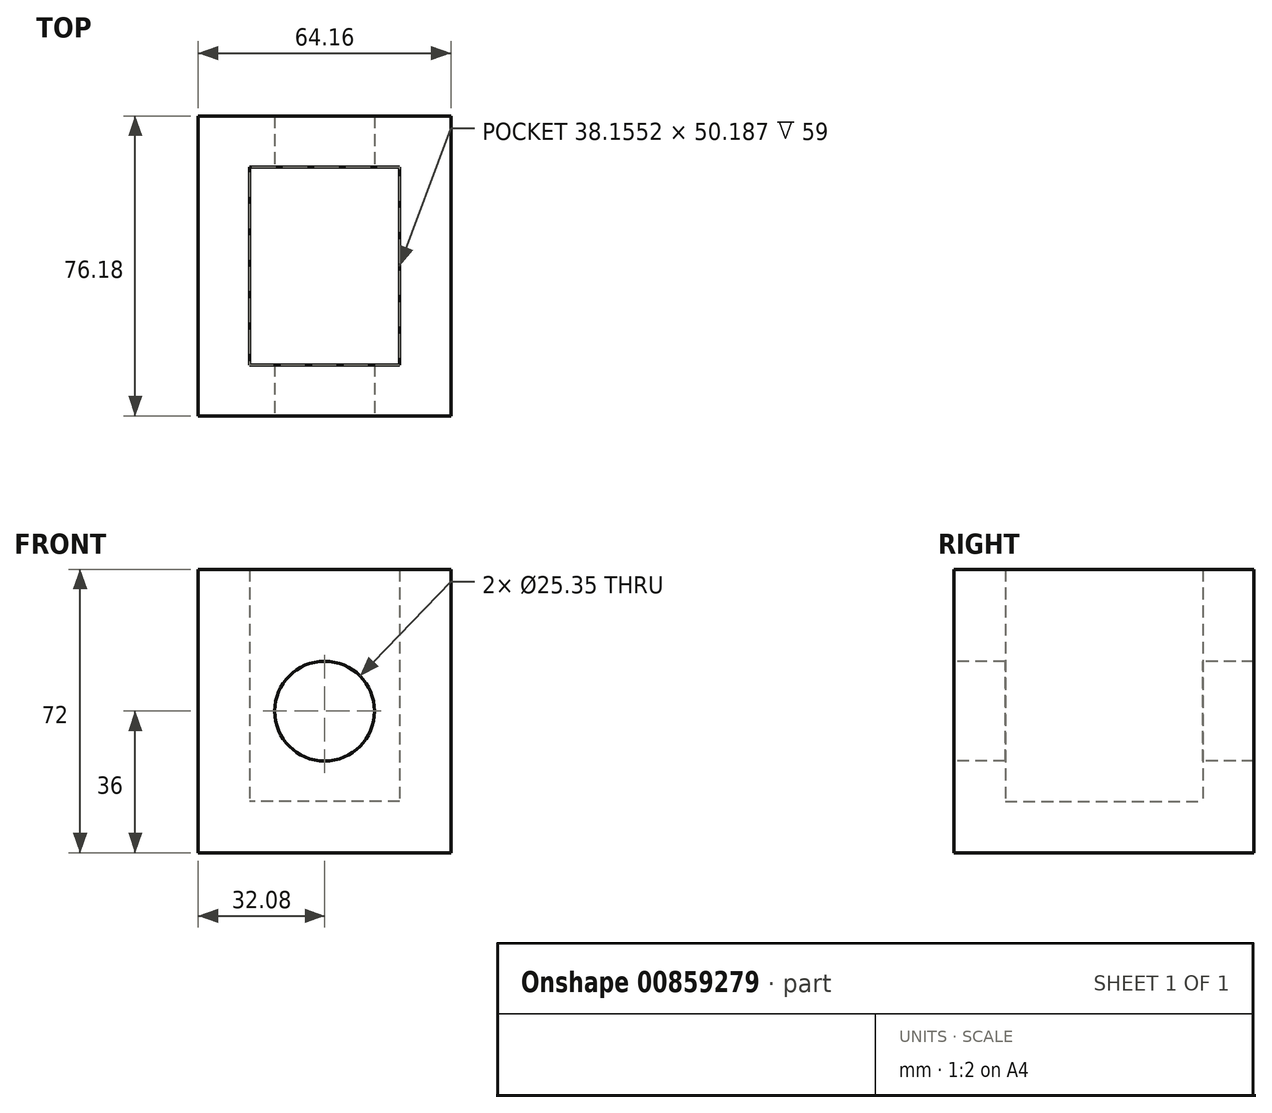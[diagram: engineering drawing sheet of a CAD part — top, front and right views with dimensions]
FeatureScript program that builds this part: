
annotation { "Feature Type Name" : "Feature", "Feature Type Description" : "" }
export const myFeature = defineFeature(function(context is Context, id is Id, definition is map)
    precondition{}
    {
        {
            var Q0;
            Q0=qCreatedBy(makeId("Top.planeOp"),FACE);
            var sketch = newSketch(context, id + "F0", { "sketchPlane" : qUnion([Q0])});
            skLineSegment(sketch, "E0.bottom", {"start": v(32.08, -38.1) * mm, "end": v(-32.08, -38.1) * mm});
            skLineSegment(sketch, "E0.top", {"start": v(32.08, 38.1) * mm, "end": v(-32.08, 38.1) * mm});
            skLineSegment(sketch, "E0.left", {"start": v(32.08, -38.1) * mm, "end": v(32.08, 38.1) * mm});
            skLineSegment(sketch, "E0.right", {"start": v(-32.08, -38.1) * mm, "end": v(-32.08, 38.1) * mm});
            skPoint(sketch, "E0.middle", {"position": v(0, 0) * mm});
            skSolve(sketch);
        }
        {
            var Q0;
            Q0=makeQuery(id+"F0.imprint","IMPRINT",FACE,{"disambiguationData":[TD([[makeQuery(id+"F0.imprint","IMPRINT",EDGE,{"derivedFrom":sQuery(id+"F0.wireOp",EDGE,"E0.bottom")}),-1.0]])]});
            extrude(context, id + "F1", {"entities" : qUnion([Q0]), "depth" : 72 * mm, "offsetDistance" : 25 * mm});
        }
        {
            var Q0;
            Q0=makeQuery(id+"F1.opExtrude","CAP_FACE",FACE,{"disambiguationData":[OSD([sQuery(id+"F0.wireOp",EDGE,"E0.bottom"),sQuery(id+"F0.wireOp",EDGE,"E0.top"),sQuery(id+"F0.wireOp",EDGE,"E0.left"),sQuery(id+"F0.wireOp",EDGE,"E0.right")])],"isStart":false});
            shell(context, id + "F2", {"entities" : qUnion([Q0]), "thickness" : 13 * mm});
        }
        {
            var Q0;
            Q0=makeQuery(id+"F1.opExtrude","SWEPT_FACE",FACE,{"disambiguationData":[OSD([sQuery(id+"F0.wireOp",EDGE,"E0.bottom")])]});
            var sketch = newSketch(context, id + "F3", { "sketchPlane" : qUnion([Q0])});
            skCircle(sketch, "E1", {"center": v(0, 36) * mm, "radius": 12.67 * mm});
            skSolve(sketch);
        }
        {
            var Q0;
            Q0=makeQuery(id+"F3.imprint","IMPRINT",FACE,{"disambiguationData":[TD([[makeQuery(id+"F3.imprint","IMPRINT",EDGE,{"derivedFrom":sQuery(id+"F3.wireOp",EDGE,"E1")}),1.0]])]});
            extrude(context, id + "F4", {"entities" : qUnion([Q0]), "operationType" : NewBodyOperationType.REMOVE, "oppositeDirection" : true, "depth" : 108.5 * mm, "offsetDistance" : 25 * mm});
        }
    });
